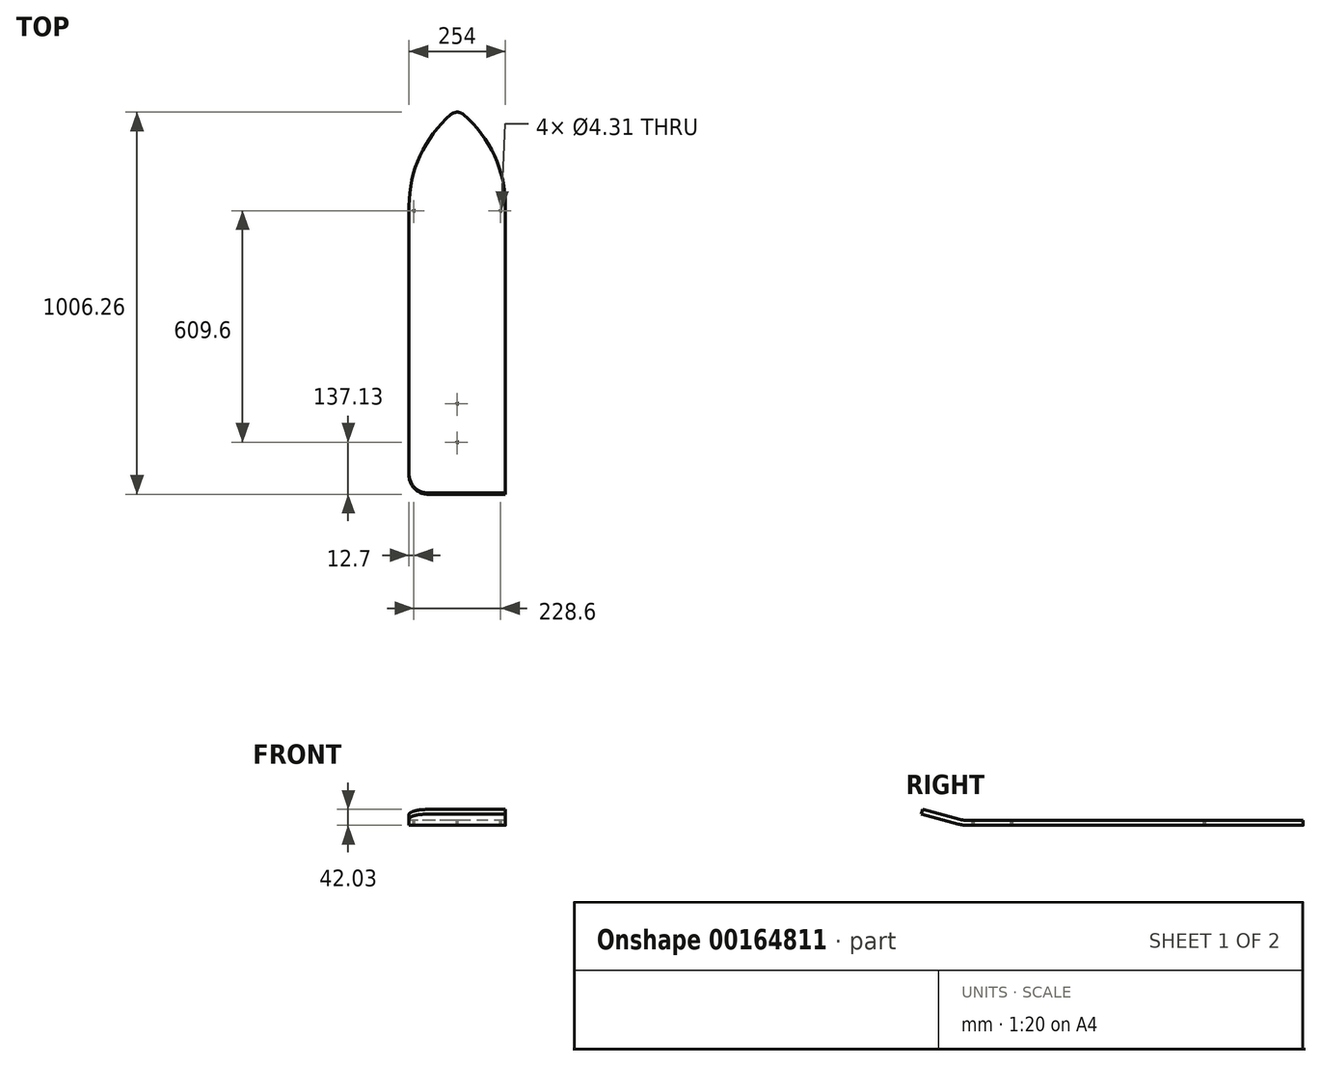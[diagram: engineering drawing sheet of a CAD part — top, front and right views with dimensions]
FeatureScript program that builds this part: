
annotation { "Feature Type Name" : "Feature", "Feature Type Description" : "" }
export const myFeature = defineFeature(function(context is Context, id is Id, definition is map)
    precondition{}
    {
        {
            var Q0;
            Q0=qCreatedBy(makeId("Top.planeOp"),FACE);
            var sketch = newSketch(context, id + "F0", { "sketchPlane" : qUnion([Q0])});
            skLineSegment(sketch, "E0.bottom", {"start": v(0, 0) * mm, "end": v(-254, 0) * mm, "construction": true});
            skLineSegment(sketch, "E0.top", {"start": v(0, -635) * mm, "end": v(-254, -635) * mm});
            skLineSegment(sketch, "E0.left", {"start": v(0, 0) * mm, "end": v(0, -635) * mm});
            skLineSegment(sketch, "E0.right", {"start": v(-254, 0) * mm, "end": v(-254, -635) * mm});
            skArc(sketch, "E1", {"start": v(0, 0) * mm, "mid": v(-33.52, 142) * mm, "end": v(-127, 254) * mm});
            skArc(sketch, "E2", {"start": v(-127, 254) * mm, "mid": v(-220.48, 142) * mm, "end": v(-254, 0) * mm});
            skLineSegment(sketch, "E3", {"start": v(-127, 0) * mm, "end": v(-127, 254) * mm, "construction": true});
            skSolve(sketch);
        }
        {
            var Q0;
            Q0 = qSketchRegion(id + "F0", true);
            extrude(context, id + "F1", {"entities" : qUnion([Q0]), "depth" : 12.7 * mm});
        }
        {
            var Q0;
            Q0=makeQuery(id+"F1.opExtrude","SWEPT_EDGE",EDGE,{"disambiguationData":[OSD([sQuery(id+"F0.wireOp",EDGE,"E1"),sQuery(id+"F0.wireOp",EDGE,"E2")])]});
            fillet(context, id + "F2", {"entities" : qUnion([Q0]), "radius" : 25.4 * mm, "tangentPropagation" : true, "allowEdgeOverflow" : false});
        }
        {
            var Q0;
            Q0=makeQuery(id+"F1.opExtrude","SWEPT_FACE",FACE,{"disambiguationData":[OSD([sQuery(id+"F0.wireOp",EDGE,"E0.right")])]});
            var sketch = newSketch(context, id + "F3", { "sketchPlane" : qUnion([Q0])});
            skArc(sketch, "E4", {"start": v(635, 12.7) * mm, "mid": v(646.6, 13.46) * mm, "end": v(658, 15.73) * mm});
            skArc(sketch, "E5", {"start": v(635, 0) * mm, "mid": v(648.26, 0.87) * mm, "end": v(661.3, 3.46) * mm});
            skLineSegment(sketch, "E6", {"start": v(635, 101.6) * mm, "end": v(658, 15.73) * mm, "construction": true});
            skLineSegment(sketch, "E7", {"start": v(658, 15.73) * mm, "end": v(661.3, 3.46) * mm, "construction": true});
            skLineSegment(sketch, "E8.bottom", {"start": v(658, 15.73) * mm, "end": v(756.15, 42.03) * mm});
            skLineSegment(sketch, "E8.top", {"start": v(661.3, 3.46) * mm, "end": v(759.43, 29.76) * mm});
            skLineSegment(sketch, "E8.right", {"start": v(756.15, 42.03) * mm, "end": v(759.43, 29.76) * mm});
            skLineSegment(sketch, "E9", {"start": v(635, 101.6) * mm, "end": v(635, 12.7) * mm, "construction": true});
            skLineSegment(sketch, "E10", {"start": v(635, 12.7) * mm, "end": v(635, 0) * mm});
            skLineSegment(sketch, "E11", {"start": v(635, 0) * mm, "end": v(759.43, 0) * mm, "construction": true});
            skLineSegment(sketch, "E12", {"start": v(759.43, 0) * mm, "end": v(759.43, 29.76) * mm, "construction": true});
            skSolve(sketch);
        }
        {
            var Q0;
            Q0 = qSketchRegion(id + "F3", true);
            var Q1;
            Q1=makeQuery(id+"F1.opExtrude","SWEPT_FACE",FACE,{"disambiguationData":[OSD([sQuery(id+"F0.wireOp",EDGE,"E0.left")])]});
            extrude(context, id + "F4", {"entities" : qUnion([Q0]), "operationType" : NewBodyOperationType.ADD, "endBound" : BoundingType.UP_TO_SURFACE, "oppositeDirection" : true, "endBoundEntityFace" : qUnion([Q1]), "depth" : 25.4 * mm});
        }
        {
            var Q0;
            Q0=makeQuery(id+"F4.opExtrude","TWEAK_EDGE",EDGE,{"derivedFrom":[makeQuery(id+"F1.opExtrude","SWEPT_FACE",FACE,{"disambiguationData":[OSD([sQuery(id+"F0.wireOp",EDGE,"E0.left")])]}),makeQuery(id+"F3.imprint","IMPRINT",EDGE,{"derivedFrom":sQuery(id+"F3.wireOp",EDGE,"E8.right")})]});
            var Q1;
            Q1=makeQuery(id+"F4.opExtrude","CAP_EDGE",EDGE,{"disambiguationData":[OSD([sQuery(id+"F3.wireOp",EDGE,"E8.right")])],"isStart":true});
            fillet(context, id + "F5", {"entities" : qUnion([Q0, Q1]), "radius" : 50.8 * mm, "tangentPropagation" : true, "allowEdgeOverflow" : false});
        }
        {
            var Q0;
            Q0=makeQuery(id+"F1.opExtrude","CAP_FACE",FACE,{"disambiguationData":[OSD([sQuery(id+"F0.wireOp",EDGE,"E0.top"),sQuery(id+"F0.wireOp",EDGE,"E0.left"),sQuery(id+"F0.wireOp",EDGE,"E0.right"),sQuery(id+"F0.wireOp",EDGE,"E1"),sQuery(id+"F0.wireOp",EDGE,"E2")])],"isStart":false});
            var sketch = newSketch(context, id + "F6", { "sketchPlane" : qUnion([Q0])});
            skLineSegment(sketch, "E13", {"start": v(-127, -520.7) * mm, "end": v(-127, -622.3) * mm, "construction": true});
            skLineSegment(sketch, "E14", {"start": v(0, 0) * mm, "end": v(-254, 0) * mm, "construction": true});
            skLineSegment(sketch, "E15", {"start": v(-127, 0) * mm, "end": v(-127, -12.7) * mm, "construction": true});
            skLineSegment(sketch, "E16", {"start": v(-12.7, -12.7) * mm, "end": v(-241.3, -12.7) * mm, "construction": true});
            skCircle(sketch, "E17", {"center": v(-127, -520.7) * mm, "radius": 2.15 * mm});
            skCircle(sketch, "E18", {"center": v(-127, -622.3) * mm, "radius": 2.15 * mm});
            skCircle(sketch, "E19", {"center": v(-241.3, -12.7) * mm, "radius": 2.15 * mm});
            skCircle(sketch, "E20", {"center": v(-12.7, -12.7) * mm, "radius": 2.15 * mm});
            skLineSegment(sketch, "E21", {"start": v(-127, -635) * mm, "end": v(-127, -622.3) * mm, "construction": true});
            skSolve(sketch);
        }
        {
            var Q0;
            Q0 = qSketchRegion(id + "F6", true);
            var Q1;
            Q1=makeQuery(id+"F1.opExtrude","CAP_FACE",FACE,{"disambiguationData":[OSD([sQuery(id+"F0.wireOp",EDGE,"E0.top"),sQuery(id+"F0.wireOp",EDGE,"E0.left"),sQuery(id+"F0.wireOp",EDGE,"E0.right"),sQuery(id+"F0.wireOp",EDGE,"E1"),sQuery(id+"F0.wireOp",EDGE,"E2")])],"isStart":true});
            extrude(context, id + "F7", {"entities" : qUnion([Q0]), "operationType" : NewBodyOperationType.REMOVE, "endBound" : BoundingType.UP_TO_SURFACE, "oppositeDirection" : true, "endBoundEntityFace" : qUnion([Q1]), "depth" : 25.4 * mm});
        }
    });
